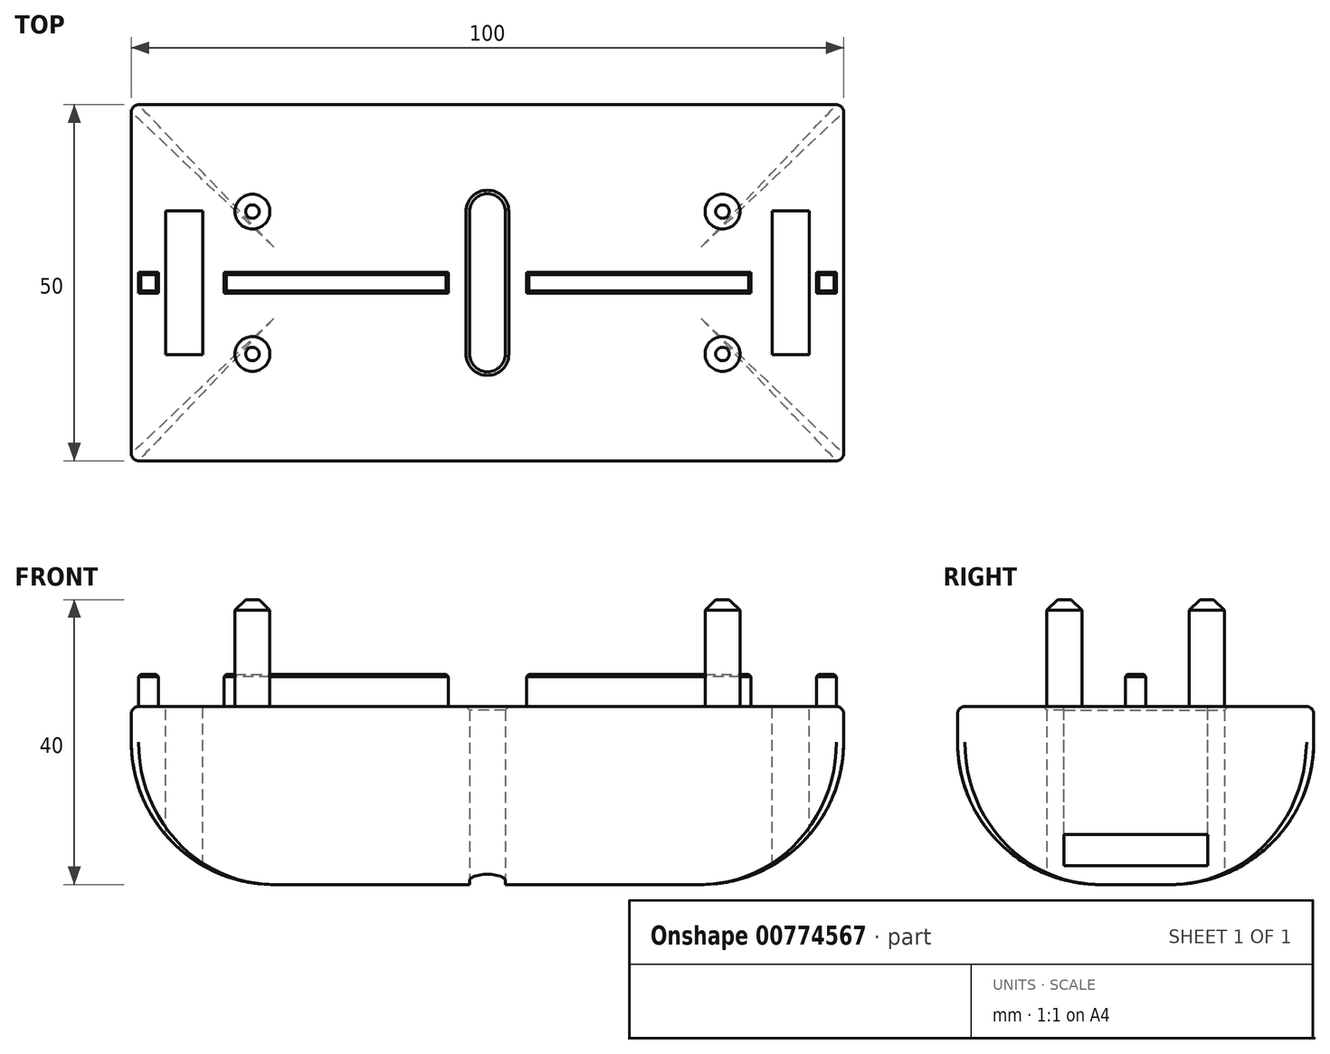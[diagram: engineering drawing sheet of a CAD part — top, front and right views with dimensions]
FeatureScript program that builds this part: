
annotation { "Feature Type Name" : "Feature", "Feature Type Description" : "" }
export const myFeature = defineFeature(function(context is Context, id is Id, definition is map)
    precondition{}
    {
        {
            var Q0;
            Q0=qCreatedBy(makeId("Top.planeOp"),FACE);
            var sketch = newSketch(context, id + "F0", { "sketchPlane" : qUnion([Q0])});
            skLineSegment(sketch, "E0.bottom", {"start": v(50, -25) * mm, "end": v(-50, -25) * mm});
            skLineSegment(sketch, "E0.top", {"start": v(50, 25) * mm, "end": v(-50, 25) * mm});
            skLineSegment(sketch, "E0.left", {"start": v(50, -25) * mm, "end": v(50, 25) * mm});
            skLineSegment(sketch, "E0.right", {"start": v(-50, -25) * mm, "end": v(-50, 25) * mm});
            skPoint(sketch, "E0.middle", {"position": v(0, 0) * mm});
            skLineSegment(sketch, "E1", {"start": v(-2.5, 0) * mm, "end": v(-2.5, 10) * mm});
            skArc(sketch, "E2", {"start": v(-2.5, 10) * mm, "mid": v(-1.77, 11.77) * mm, "end": v(0, 12.5) * mm});
            skLineSegment(sketch, "E3.MirrorCS", {"start": v(2.5, 0) * mm, "end": v(2.5, 10) * mm});
            skArc(sketch, "E4.MirrorCS", {"start": v(2.5, 10) * mm, "mid": v(1.77, 11.77) * mm, "end": v(0, 12.5) * mm});
            skArc(sketch, "E5.MirrorCS", {"start": v(2.5, -10) * mm, "mid": v(1.77, -11.77) * mm, "end": v(0, -12.5) * mm});
            skLineSegment(sketch, "E6.MirrorCS", {"start": v(2.5, 0) * mm, "end": v(2.5, -10) * mm});
            skArc(sketch, "E7.MirrorCS", {"start": v(-2.5, -10) * mm, "mid": v(-1.77, -11.77) * mm, "end": v(0, -12.5) * mm});
            skLineSegment(sketch, "E8.MirrorCS", {"start": v(-2.5, 0) * mm, "end": v(-2.5, -10) * mm});
            skSolve(sketch);
        }
        {
            var Q0;
            Q0 = qSketchRegion(id + "F0", true);
            extrude(context, id + "F1", {"entities" : qUnion([Q0]), "depth" : 25 * mm, "offsetDistance" : 25 * mm});
        }
        {
            var Q0;
            Q0=makeQuery(id+"F1.opExtrude","CAP_FACE",FACE,{"disambiguationData":[OSD([sQuery(id+"F0.wireOp",EDGE,"E0.bottom"),sQuery(id+"F0.wireOp",EDGE,"E0.top"),sQuery(id+"F0.wireOp",EDGE,"E0.left"),sQuery(id+"F0.wireOp",EDGE,"E0.right"),sQuery(id+"F0.wireOp",EDGE,"E1"),sQuery(id+"F0.wireOp",EDGE,"E2"),sQuery(id+"F0.wireOp",EDGE,"E3.MirrorCS"),sQuery(id+"F0.wireOp",EDGE,"E4.MirrorCS"),sQuery(id+"F0.wireOp",EDGE,"E5.MirrorCS"),sQuery(id+"F0.wireOp",EDGE,"E6.MirrorCS"),sQuery(id+"F0.wireOp",EDGE,"E7.MirrorCS"),sQuery(id+"F0.wireOp",EDGE,"E8.MirrorCS")])],"isStart":false});
            var sketch = newSketch(context, id + "F2", { "sketchPlane" : qUnion([Q0])});
            skCircle(sketch, "E9", {"center": v(-33, 10) * mm, "radius": 2.45 * mm});
            skCircle(sketch, "E10.MirrorC", {"center": v(33, 10) * mm, "radius": 2.45 * mm});
            skCircle(sketch, "E11.MirrorC", {"center": v(-33, -10) * mm, "radius": 2.45 * mm});
            skCircle(sketch, "E12.MirrorC", {"center": v(33, -10) * mm, "radius": 2.45 * mm});
            skSolve(sketch);
        }
        {
            var Q0;
            Q0 = qSketchRegion(id + "F2", true);
            extrude(context, id + "F3", {"entities" : qUnion([Q0]), "operationType" : NewBodyOperationType.ADD, "depth" : 15 * mm, "offsetDistance" : 25 * mm});
        }
        {
            var Q0;
            Q0=makeQuery(id+"F3.opExtrude","CAP_EDGE",EDGE,{"disambiguationData":[OSD([sQuery(id+"F2.wireOp",EDGE,"E9")])],"isStart":false});
            var Q1;
            Q1=makeQuery(id+"F3.opExtrude","CAP_EDGE",EDGE,{"disambiguationData":[OSD([sQuery(id+"F2.wireOp",EDGE,"E11.MirrorC")])],"isStart":false});
            var Q2;
            Q2=makeQuery(id+"F3.opExtrude","CAP_EDGE",EDGE,{"disambiguationData":[OSD([sQuery(id+"F2.wireOp",EDGE,"E10.MirrorC")])],"isStart":false});
            var Q3;
            Q3=makeQuery(id+"F3.opExtrude","CAP_EDGE",EDGE,{"disambiguationData":[OSD([sQuery(id+"F2.wireOp",EDGE,"E12.MirrorC")])],"isStart":false});
            chamfer(context, id + "F4", {"entities" : qUnion([Q0, Q1, Q2, Q3]), "width" : 1.5 * mm, "tangentPropagation" : true});
        }
        {
            var Q0;
            Q0=makeQuery(id+"F1.opExtrude","CAP_FACE",FACE,{"disambiguationData":[OSD([sQuery(id+"F0.wireOp",EDGE,"E0.bottom"),sQuery(id+"F0.wireOp",EDGE,"E0.top"),sQuery(id+"F0.wireOp",EDGE,"E0.left"),sQuery(id+"F0.wireOp",EDGE,"E0.right"),sQuery(id+"F0.wireOp",EDGE,"E1"),sQuery(id+"F0.wireOp",EDGE,"E2"),sQuery(id+"F0.wireOp",EDGE,"E3.MirrorCS"),sQuery(id+"F0.wireOp",EDGE,"E4.MirrorCS"),sQuery(id+"F0.wireOp",EDGE,"E5.MirrorCS"),sQuery(id+"F0.wireOp",EDGE,"E6.MirrorCS"),sQuery(id+"F0.wireOp",EDGE,"E7.MirrorCS"),sQuery(id+"F0.wireOp",EDGE,"E8.MirrorCS")])],"isStart":false});
            var sketch = newSketch(context, id + "F5", { "sketchPlane" : qUnion([Q0])});
            skLineSegment(sketch, "E13.bottom", {"start": v(-45.2, 10.1) * mm, "end": v(-40, 10.1) * mm});
            skLineSegment(sketch, "E13.top", {"start": v(-45.2, -10.1) * mm, "end": v(-40, -10.1) * mm});
            skLineSegment(sketch, "E13.left", {"start": v(-45.2, 10.1) * mm, "end": v(-45.2, -10.1) * mm});
            skLineSegment(sketch, "E13.right", {"start": v(-40, 10.1) * mm, "end": v(-40, -10.1) * mm});
            skPoint(sketch, "E13.middle", {"position": v(-42.6, 0) * mm});
            skLineSegment(sketch, "E14.MirrorCS", {"start": v(45.2, 10.1) * mm, "end": v(40, 10.1) * mm});
            skPoint(sketch, "E15.MirrorP", {"position": v(42.6, 0) * mm});
            skLineSegment(sketch, "E16.MirrorCS", {"start": v(45.2, -10.1) * mm, "end": v(40, -10.1) * mm});
            skLineSegment(sketch, "E17.MirrorCS", {"start": v(45.2, 10.1) * mm, "end": v(45.2, -10.1) * mm});
            skLineSegment(sketch, "E18.MirrorCS", {"start": v(40, 10.1) * mm, "end": v(40, -10.1) * mm});
            skSolve(sketch);
        }
        {
            var Q0;
            Q0 = qSketchRegion(id + "F5", true);
            extrude(context, id + "F6", {"entities" : qUnion([Q0]), "operationType" : NewBodyOperationType.REMOVE, "endBound" : BoundingType.THROUGH_ALL, "oppositeDirection" : true, "depth" : 25 * mm, "offsetDistance" : 25 * mm});
        }
        {
            var Q0;
            Q0=makeQuery(id+"F1.opExtrude","CAP_FACE",FACE,{"disambiguationData":[OSD([sQuery(id+"F0.wireOp",EDGE,"E0.bottom"),sQuery(id+"F0.wireOp",EDGE,"E0.top"),sQuery(id+"F0.wireOp",EDGE,"E0.left"),sQuery(id+"F0.wireOp",EDGE,"E0.right"),sQuery(id+"F0.wireOp",EDGE,"E1"),sQuery(id+"F0.wireOp",EDGE,"E2"),sQuery(id+"F0.wireOp",EDGE,"E3.MirrorCS"),sQuery(id+"F0.wireOp",EDGE,"E4.MirrorCS"),sQuery(id+"F0.wireOp",EDGE,"E5.MirrorCS"),sQuery(id+"F0.wireOp",EDGE,"E6.MirrorCS"),sQuery(id+"F0.wireOp",EDGE,"E7.MirrorCS"),sQuery(id+"F0.wireOp",EDGE,"E8.MirrorCS")])],"isStart":false});
            var sketch = newSketch(context, id + "F7", { "sketchPlane" : qUnion([Q0])});
            skLineSegment(sketch, "E19.bottom", {"start": v(-46.2, -1.45) * mm, "end": v(-49, -1.45) * mm});
            skLineSegment(sketch, "E19.top", {"start": v(-46.2, 1.45) * mm, "end": v(-49, 1.45) * mm});
            skLineSegment(sketch, "E19.left", {"start": v(-46.2, -1.45) * mm, "end": v(-46.2, 1.45) * mm});
            skLineSegment(sketch, "E19.right", {"start": v(-49, -1.45) * mm, "end": v(-49, 1.45) * mm});
            skPoint(sketch, "E19.middle", {"position": v(-47.6, 0) * mm});
            skPoint(sketch, "E19.middle.positionSnap0", {"position": v(-45.2, 0) * mm});
            skPoint(sketch, "E19.centerSnap0", {"position": v(-45.2, 0) * mm});
            skLineSegment(sketch, "E20.bottom", {"start": v(-5.5, -1.45) * mm, "end": v(-37, -1.45) * mm});
            skLineSegment(sketch, "E20.top", {"start": v(-5.5, 1.45) * mm, "end": v(-37, 1.45) * mm});
            skLineSegment(sketch, "E20.left", {"start": v(-5.5, -1.45) * mm, "end": v(-5.5, 1.45) * mm});
            skLineSegment(sketch, "E20.right", {"start": v(-37, -1.45) * mm, "end": v(-37, 1.45) * mm});
            skPoint(sketch, "E20.middle", {"position": v(-21.25, 0) * mm});
            skLineSegment(sketch, "E21.MirrorCS", {"start": v(46.2, 1.45) * mm, "end": v(49, 1.45) * mm});
            skLineSegment(sketch, "E22.MirrorCS", {"start": v(46.2, -1.45) * mm, "end": v(49, -1.45) * mm});
            skPoint(sketch, "E23.MirrorP", {"position": v(47.6, 0) * mm});
            skLineSegment(sketch, "E24.MirrorCS", {"start": v(49, -1.45) * mm, "end": v(49, 1.45) * mm});
            skLineSegment(sketch, "E25.MirrorCS", {"start": v(46.2, -1.45) * mm, "end": v(46.2, 1.45) * mm});
            skLineSegment(sketch, "E26.MirrorCS", {"start": v(5.5, -1.45) * mm, "end": v(5.5, 1.45) * mm});
            skLineSegment(sketch, "E27.MirrorCS", {"start": v(37, -1.45) * mm, "end": v(37, 1.45) * mm});
            skPoint(sketch, "E28.MirrorP", {"position": v(21.25, 0) * mm});
            skLineSegment(sketch, "E29.MirrorCS", {"start": v(5.5, -1.45) * mm, "end": v(37, -1.45) * mm});
            skLineSegment(sketch, "E30.MirrorCS", {"start": v(5.5, 1.45) * mm, "end": v(37, 1.45) * mm});
            skSolve(sketch);
        }
        {
            var Q0;
            Q0 = qSketchRegion(id + "F7", true);
            extrude(context, id + "F8", {"entities" : qUnion([Q0]), "operationType" : NewBodyOperationType.ADD, "depth" : 4.5 * mm, "offsetDistance" : 25 * mm});
        }
        {
            var Q0;
            Q0=makeQuery(id+"F8.opExtrude","CAP_EDGE",EDGE,{"disambiguationData":[OSD([sQuery(id+"F7.wireOp",EDGE,"E22.MirrorCS")])],"isStart":false});
            var Q1;
            Q1=makeQuery(id+"F8.opExtrude","CAP_EDGE",EDGE,{"disambiguationData":[OSD([sQuery(id+"F7.wireOp",EDGE,"E25.MirrorCS")])],"isStart":false});
            var Q2;
            Q2=makeQuery(id+"F8.opExtrude","CAP_EDGE",EDGE,{"disambiguationData":[OSD([sQuery(id+"F7.wireOp",EDGE,"E24.MirrorCS")])],"isStart":false});
            var Q3;
            Q3=makeQuery(id+"F8.opExtrude","CAP_EDGE",EDGE,{"disambiguationData":[OSD([sQuery(id+"F7.wireOp",EDGE,"E21.MirrorCS")])],"isStart":false});
            var Q4;
            Q4=makeQuery(id+"F8.opExtrude","CAP_EDGE",EDGE,{"disambiguationData":[OSD([sQuery(id+"F7.wireOp",EDGE,"E27.MirrorCS")])],"isStart":false});
            var Q5;
            Q5=makeQuery(id+"F8.opExtrude","CAP_EDGE",EDGE,{"disambiguationData":[OSD([sQuery(id+"F7.wireOp",EDGE,"E29.MirrorCS")])],"isStart":false});
            var Q6;
            Q6=makeQuery(id+"F8.opExtrude","CAP_EDGE",EDGE,{"disambiguationData":[OSD([sQuery(id+"F7.wireOp",EDGE,"E30.MirrorCS")])],"isStart":false});
            var Q7;
            Q7=makeQuery(id+"F8.opExtrude","CAP_EDGE",EDGE,{"disambiguationData":[OSD([sQuery(id+"F7.wireOp",EDGE,"E26.MirrorCS")])],"isStart":false});
            var Q8;
            Q8=makeQuery(id+"F8.opExtrude","CAP_EDGE",EDGE,{"disambiguationData":[OSD([sQuery(id+"F7.wireOp",EDGE,"E20.left")])],"isStart":false});
            var Q9;
            Q9=makeQuery(id+"F8.opExtrude","CAP_EDGE",EDGE,{"disambiguationData":[OSD([sQuery(id+"F7.wireOp",EDGE,"E20.bottom")])],"isStart":false});
            var Q10;
            Q10=makeQuery(id+"F8.opExtrude","CAP_EDGE",EDGE,{"disambiguationData":[OSD([sQuery(id+"F7.wireOp",EDGE,"E20.top")])],"isStart":false});
            var Q11;
            Q11=makeQuery(id+"F8.opExtrude","CAP_EDGE",EDGE,{"disambiguationData":[OSD([sQuery(id+"F7.wireOp",EDGE,"E20.right")])],"isStart":false});
            var Q12;
            Q12=makeQuery(id+"F8.opExtrude","CAP_EDGE",EDGE,{"disambiguationData":[OSD([sQuery(id+"F7.wireOp",EDGE,"E19.bottom")])],"isStart":false});
            var Q13;
            Q13=makeQuery(id+"F8.opExtrude","CAP_EDGE",EDGE,{"disambiguationData":[OSD([sQuery(id+"F7.wireOp",EDGE,"E19.left")])],"isStart":false});
            var Q14;
            Q14=makeQuery(id+"F8.opExtrude","CAP_EDGE",EDGE,{"disambiguationData":[OSD([sQuery(id+"F7.wireOp",EDGE,"E19.top")])],"isStart":false});
            var Q15;
            Q15=makeQuery(id+"F8.opExtrude","CAP_EDGE",EDGE,{"disambiguationData":[OSD([sQuery(id+"F7.wireOp",EDGE,"E19.right")])],"isStart":false});
            chamfer(context, id + "F9", {"entities" : qUnion([Q0, Q1, Q2, Q3, Q4, Q5, Q6, Q7, Q8, Q9, Q10, Q11, Q12, Q13, Q14, Q15]), "width" : 0.3 * mm, "tangentPropagation" : true});
        }
        {
            var Q0;
            Q0=makeQuery(id+"F1.opExtrude","CAP_EDGE",EDGE,{"disambiguationData":[OSD([sQuery(id+"F0.wireOp",EDGE,"E0.top")])],"isStart":false});
            var Q1;
            Q1=makeQuery(id+"F1.opExtrude","CAP_EDGE",EDGE,{"disambiguationData":[OSD([sQuery(id+"F0.wireOp",EDGE,"E0.right")])],"isStart":false});
            var Q2;
            Q2=makeQuery(id+"F1.opExtrude","CAP_EDGE",EDGE,{"disambiguationData":[OSD([sQuery(id+"F0.wireOp",EDGE,"E0.bottom")])],"isStart":false});
            var Q3;
            Q3=makeQuery(id+"F1.opExtrude","CAP_EDGE",EDGE,{"disambiguationData":[OSD([sQuery(id+"F0.wireOp",EDGE,"E0.left")])],"isStart":false});
            var Q4;
            Q4=makeQuery(id+"F1.opExtrude","SWEPT_EDGE",EDGE,{"disambiguationData":[OSD([sQuery(id+"F0.wireOp",EDGE,"E0.bottom"),sQuery(id+"F0.wireOp",EDGE,"E0.left")])]});
            var Q5;
            Q5=makeQuery(id+"F1.opExtrude","SWEPT_EDGE",EDGE,{"disambiguationData":[OSD([sQuery(id+"F0.wireOp",EDGE,"E0.top"),sQuery(id+"F0.wireOp",EDGE,"E0.left")])]});
            var Q6;
            Q6=makeQuery(id+"F1.opExtrude","SWEPT_EDGE",EDGE,{"disambiguationData":[OSD([sQuery(id+"F0.wireOp",EDGE,"E0.bottom"),sQuery(id+"F0.wireOp",EDGE,"E0.right")])]});
            var Q7;
            Q7=makeQuery(id+"F1.opExtrude","SWEPT_EDGE",EDGE,{"disambiguationData":[OSD([sQuery(id+"F0.wireOp",EDGE,"E0.top"),sQuery(id+"F0.wireOp",EDGE,"E0.right")])]});
            fillet(context, id + "F10", {"entities" : qUnion([Q0, Q1, Q2, Q3, Q4, Q5, Q6, Q7]), "radius" : 1 * mm, "tangentPropagation" : true, "allowEdgeOverflow" : false});
        }
        {
            var Q0;
            Q0=makeQuery(id+"F1.opExtrude","CAP_EDGE",EDGE,{"disambiguationData":[OSD([sQuery(id+"F0.wireOp",EDGE,"E1"),sQuery(id+"F0.wireOp",EDGE,"E8.MirrorCS")])],"isStart":false});
            var Q1;
            Q1=makeQuery(id+"F1.opExtrude","CAP_EDGE",EDGE,{"disambiguationData":[OSD([sQuery(id+"F0.wireOp",EDGE,"E3.MirrorCS"),sQuery(id+"F0.wireOp",EDGE,"E6.MirrorCS")])],"isStart":false});
            var Q2;
            Q2=makeQuery(id+"F1.opExtrude","CAP_EDGE",EDGE,{"disambiguationData":[OSD([sQuery(id+"F0.wireOp",EDGE,"E2"),sQuery(id+"F0.wireOp",EDGE,"E4.MirrorCS")])],"isStart":false});
            var Q3;
            Q3=makeQuery(id+"F1.opExtrude","CAP_EDGE",EDGE,{"disambiguationData":[OSD([sQuery(id+"F0.wireOp",EDGE,"E5.MirrorCS"),sQuery(id+"F0.wireOp",EDGE,"E7.MirrorCS")])],"isStart":false});
            var Q4;
            Q4=makeQuery(id+"F6.boolean.opBoolean","COPY",EDGE,{"derivedFrom":makeQuery(id+"F6.opExtrude","CAP_EDGE",EDGE,{"disambiguationData":[OSD([sQuery(id+"F5.wireOp",EDGE,"E13.left")])],"isStart":true})});
            var Q5;
            Q5=makeQuery(id+"F6.boolean.opBoolean","COPY",EDGE,{"derivedFrom":makeQuery(id+"F6.opExtrude","CAP_EDGE",EDGE,{"disambiguationData":[OSD([sQuery(id+"F5.wireOp",EDGE,"E13.top")])],"isStart":true})});
            var Q6;
            Q6=makeQuery(id+"F6.boolean.opBoolean","COPY",EDGE,{"derivedFrom":makeQuery(id+"F6.opExtrude","CAP_EDGE",EDGE,{"disambiguationData":[OSD([sQuery(id+"F5.wireOp",EDGE,"E13.right")])],"isStart":true})});
            var Q7;
            Q7=makeQuery(id+"F6.boolean.opBoolean","COPY",EDGE,{"derivedFrom":makeQuery(id+"F6.opExtrude","CAP_EDGE",EDGE,{"disambiguationData":[OSD([sQuery(id+"F5.wireOp",EDGE,"E13.bottom")])],"isStart":true})});
            var Q8;
            Q8=makeQuery(id+"F6.boolean.opBoolean","COPY",EDGE,{"derivedFrom":makeQuery(id+"F6.opExtrude","CAP_EDGE",EDGE,{"disambiguationData":[OSD([sQuery(id+"F5.wireOp",EDGE,"E16.MirrorCS")])],"isStart":true})});
            var Q9;
            Q9=makeQuery(id+"F6.boolean.opBoolean","COPY",EDGE,{"derivedFrom":makeQuery(id+"F6.opExtrude","CAP_EDGE",EDGE,{"disambiguationData":[OSD([sQuery(id+"F5.wireOp",EDGE,"E18.MirrorCS")])],"isStart":true})});
            var Q10;
            Q10=makeQuery(id+"F6.boolean.opBoolean","COPY",EDGE,{"derivedFrom":makeQuery(id+"F6.opExtrude","CAP_EDGE",EDGE,{"disambiguationData":[OSD([sQuery(id+"F5.wireOp",EDGE,"E17.MirrorCS")])],"isStart":true})});
            var Q11;
            Q11=makeQuery(id+"F6.boolean.opBoolean","COPY",EDGE,{"derivedFrom":makeQuery(id+"F6.opExtrude","CAP_EDGE",EDGE,{"disambiguationData":[OSD([sQuery(id+"F5.wireOp",EDGE,"E14.MirrorCS")])],"isStart":true})});
            chamfer(context, id + "F11", {"entities" : qUnion([Q0, Q1, Q2, Q3, Q4, Q5, Q6, Q7, Q8, Q9, Q10, Q11]), "width" : 0.5 * mm, "tangentPropagation" : true});
        }
        {
            var Q0;
            Q0=makeQuery(id+"F1.opExtrude","CAP_EDGE",EDGE,{"disambiguationData":[OSD([sQuery(id+"F0.wireOp",EDGE,"E0.bottom")])],"isStart":true});
            var Q1;
            Q1=makeQuery(id+"F1.opExtrude","CAP_EDGE",EDGE,{"disambiguationData":[OSD([sQuery(id+"F0.wireOp",EDGE,"E0.top")])],"isStart":true});
            fillet(context, id + "F12", {"entities" : qUnion([Q0, Q1]), "radius" : 20 * mm, "tangentPropagation" : true, "allowEdgeOverflow" : false});
        }
    });
